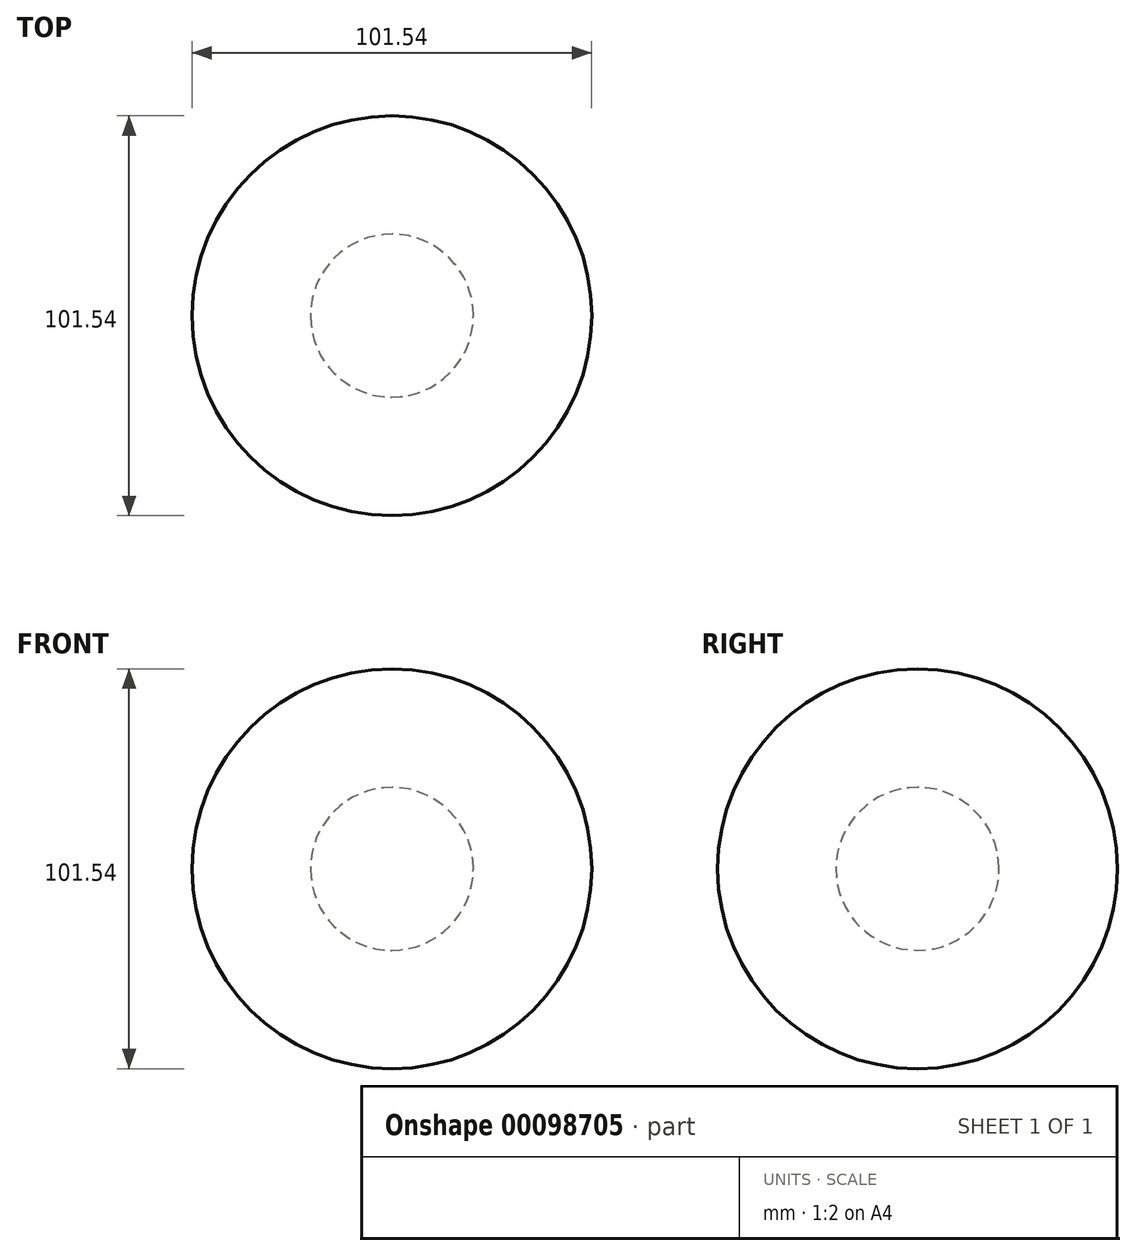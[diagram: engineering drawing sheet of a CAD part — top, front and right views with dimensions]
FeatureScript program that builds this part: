
annotation { "Feature Type Name" : "Feature", "Feature Type Description" : "" }
export const myFeature = defineFeature(function(context is Context, id is Id, definition is map)
    precondition{}
    {
        {
            var Q0;
            Q0=qCreatedBy(makeId("Front.planeOp"),FACE);
            var sketch = newSketch(context, id + "F0", { "sketchPlane" : qUnion([Q0])});
            skArc(sketch, "E0", {"start": v(-50.77, 0) * mm, "mid": v(0, 50.77) * mm, "end": v(50.77, 0) * mm});
            skLineSegment(sketch, "E1", {"start": v(-50.77, 0) * mm, "end": v(50.77, 0) * mm});
            skCircle(sketch, "E2", {"center": v(0, 0) * mm, "radius": 20.7 * mm});
            skSolve(sketch);
        }
        {
            var Q0;
            Q0 = qSketchRegion(id + "F0", true);
            var Q1;
            Q1=makeQuery(id+"F0.imprint","IMPRINT",FACE,{"disambiguationData":[TD([[makeQuery(id+"F0.imprint","IMPRINT",EDGE,{"derivedFrom":sQuery(id+"F0.wireOp",EDGE,"E0")}),-1.0]])]});
            var Q2;
            Q2=sQuery(id+"F0.wireOp",EDGE,"E1");
            revolve(context, id + "F1", {"entities" : qUnion([Q0, Q1]), "axis" : qUnion([Q2]), "revolveType" : RevolveType.FULL});
        }
    });
